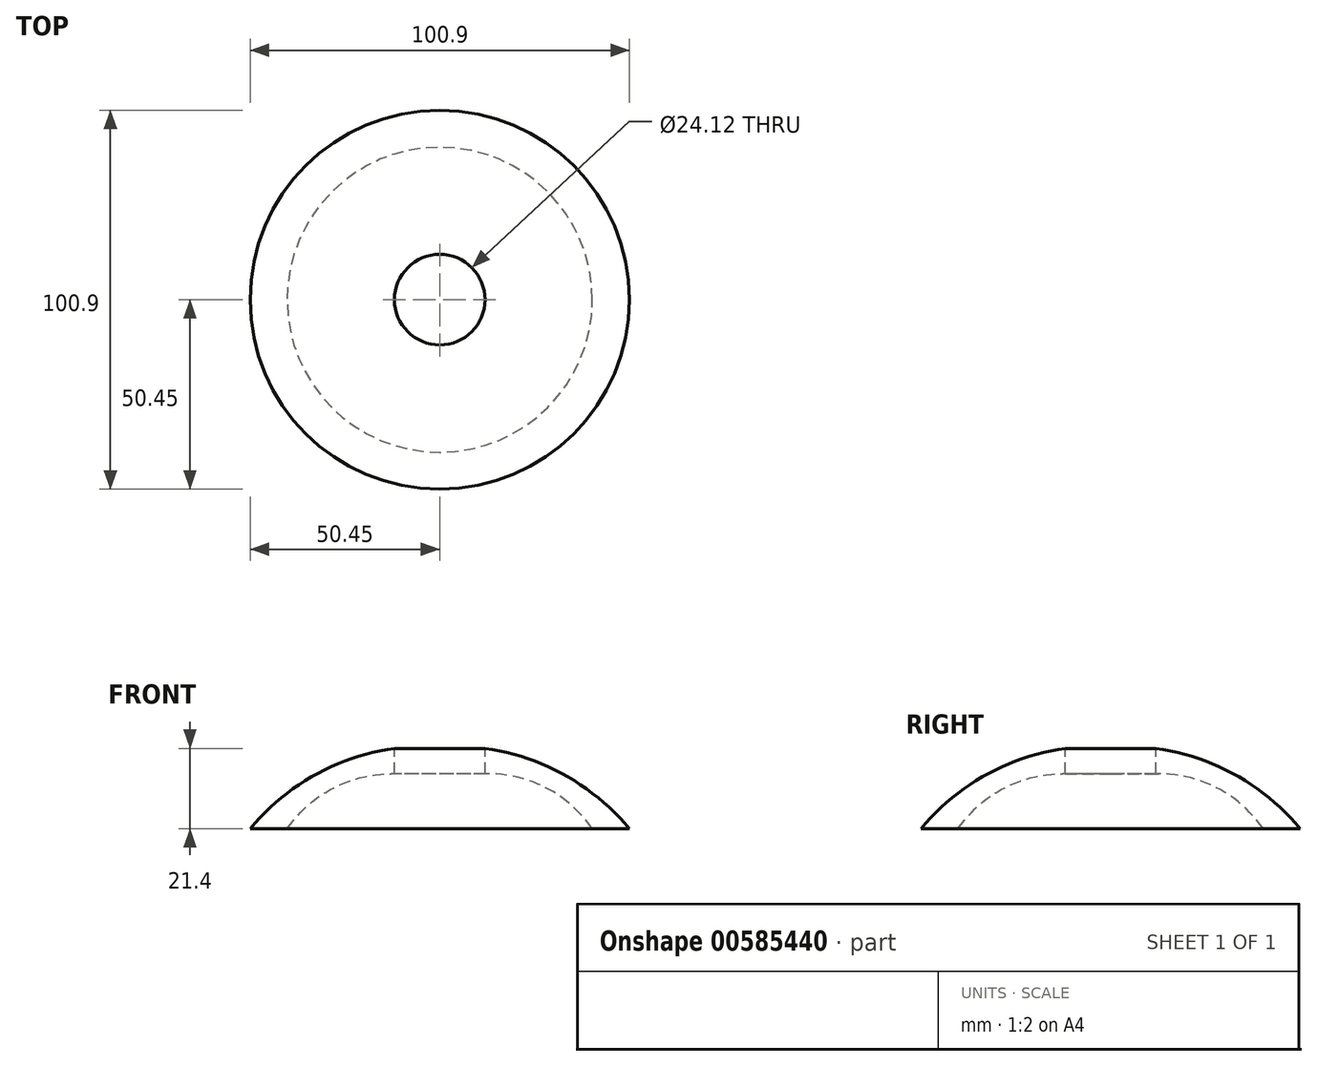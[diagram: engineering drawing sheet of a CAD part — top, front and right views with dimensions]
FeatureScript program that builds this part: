
annotation { "Feature Type Name" : "Feature", "Feature Type Description" : "" }
export const myFeature = defineFeature(function(context is Context, id is Id, definition is map)
    precondition{}
    {
        {
            var Q0;
            Q0=qCreatedBy(makeId("Front.planeOp"),FACE);
            var sketch = newSketch(context, id + "F0", { "sketchPlane" : qUnion([Q0])});
            skLineSegment(sketch, "E0", {"start": v(0, 34.31) * mm, "end": v(0, -28.54) * mm});
            skLineSegment(sketch, "E1", {"start": v(12.06, 21.4) * mm, "end": v(12.06, 14.6) * mm});
            skArc(sketch, "E2", {"start": v(40.6, 0) * mm, "mid": v(28.18, 10.92) * mm, "end": v(12.06, 14.6) * mm});
            skArc(sketch, "E3", {"start": v(50.45, 0) * mm, "mid": v(33.25, 14.28) * mm, "end": v(12.06, 21.4) * mm});
            skLineSegment(sketch, "E4", {"start": v(40.6, 0) * mm, "end": v(50.45, 0) * mm});
            skSolve(sketch);
        }
        {
            var Q0;
            Q0 = qSketchRegion(id + "F0", true);
            var Q1;
            Q1=sQuery(id+"F0.wireOp",EDGE,"E0");
            revolve(context, id + "F1", {"entities" : qUnion([Q0]), "axis" : qUnion([Q1]), "revolveType" : RevolveType.FULL});
        }
    });
